# Revit family: #window head-jamb
name_source: partatom
category: Detail Items
revit_build: Autodesk Revit 2017 (Build: 20160225_1515(x64)
units: mm (PartAtom-declared; Revit-internal decimal feet)

## family parameters
Rotate with component = No
Section Shape = Not Defined
Shared = No

## types (2) — shared parameters
facing depth = 8 mm  [stored 0.0262467 ft]
frame depth = 38 mm  [stored 0.124672 ft]
frame gap = 5 mm  [stored 0.0164042 ft]
frame rebate depth = 13 mm
frame tolerance = 10 mm  [stored 0.0328084 ft]
frame width = 92 mm  [stored 0.301837 ft]
gl-1 = 16 mm  [stored 0.0524934 ft]
gl-2 = 4 mm  [stored 0.0131234 ft]
gl-3 = 16 mm  [stored 0.0524934 ft]
gl-4 = 6 mm
gl-5 = 10 mm  [stored 0.0328084 ft]
profile depth = 61 mm
profile width = 63 mm  [stored 0.206693 ft]
seal w = 10 mm  [stored 0.0328084 ft]

## per-type parameters (varying)
| type | Type Comments | facing to frame |
| faced frame type 01 | 45-25-99 Windows | Yes |
| non faced frame 01 |  | No |

note: [stored X ft] marks values corroborated as IEEE doubles in the binary element streams (Revit-internal decimal feet)

## geometry (parser evidence)
native form markers: Blend x2, Sweep x1
no freeform markers — native parametric forms only
